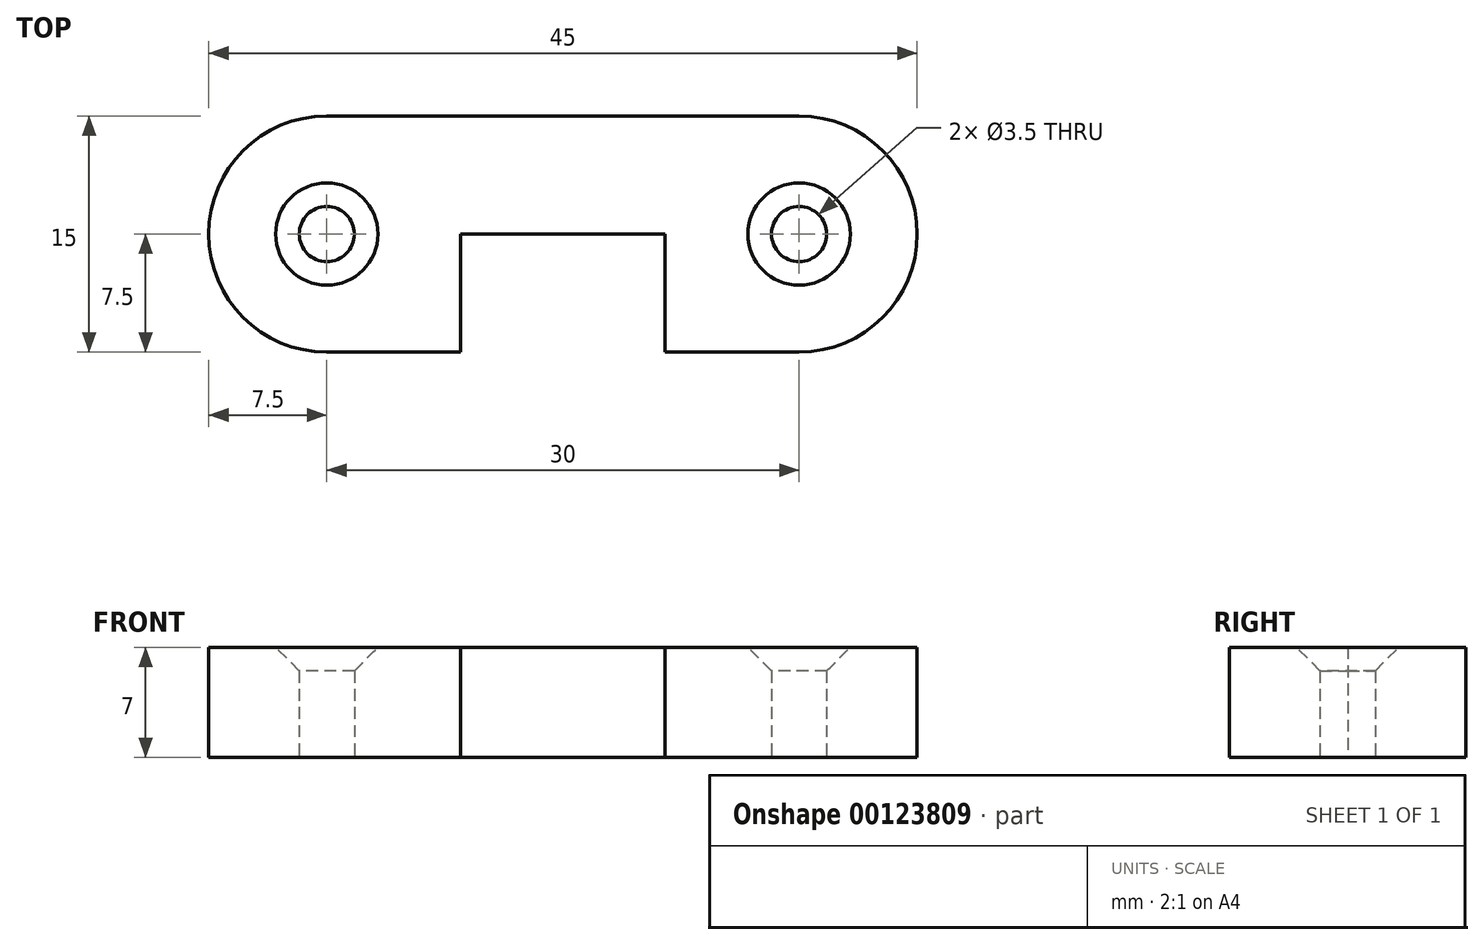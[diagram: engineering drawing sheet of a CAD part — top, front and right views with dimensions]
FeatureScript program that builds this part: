
annotation { "Feature Type Name" : "Feature", "Feature Type Description" : "" }
export const myFeature = defineFeature(function(context is Context, id is Id, definition is map)
    precondition{}
    {
        {
            var Q0;
            Q0=qCreatedBy(makeId("Top.planeOp"),FACE);
            var sketch = newSketch(context, id + "F0", { "sketchPlane" : qUnion([Q0])});
            skLineSegment(sketch, "E0.bottom", {"start": v(7.5, 7.5) * mm, "end": v(-7.5, 7.5) * mm});
            skLineSegment(sketch, "E0.top", {"start": v(7.5, -7.5) * mm, "end": v(-7.5, -7.5) * mm});
            skLineSegment(sketch, "E0.left", {"start": v(7.5, 7.5) * mm, "end": v(7.5, -7.5) * mm});
            skLineSegment(sketch, "E0.right", {"start": v(-7.5, 7.5) * mm, "end": v(-7.5, -7.5) * mm});
            skPoint(sketch, "E0.middle", {"position": v(0, 0) * mm});
            skLineSegment(sketch, "E1", {"start": v(-7.5, 7.5) * mm, "end": v(-15, 7.5) * mm});
            skLineSegment(sketch, "E2", {"start": v(-7.5, -7.5) * mm, "end": v(-15, -7.5) * mm});
            skLineSegment(sketch, "E3", {"start": v(7.5, -7.5) * mm, "end": v(15, -7.5) * mm});
            skLineSegment(sketch, "E4", {"start": v(7.5, 7.5) * mm, "end": v(15, 7.5) * mm});
            skArc(sketch, "E5", {"start": v(-15, 7.5) * mm, "mid": v(-22.5, 0) * mm, "end": v(-15, -7.5) * mm});
            skPoint(sketch, "E5.first.point", {"position": v(-7.5, 0) * mm});
            skPoint(sketch, "E5.second.point", {"position": v(-15, 7.5) * mm});
            skPoint(sketch, "E5.third.point", {"position": v(-15, -7.5) * mm});
            skArc(sketch, "E6", {"start": v(15, -7.5) * mm, "mid": v(22.5, 0) * mm, "end": v(15, 7.5) * mm});
            skPoint(sketch, "E6.first.point", {"position": v(7.5, 0) * mm});
            skPoint(sketch, "E6.second.point", {"position": v(15, 7.5) * mm});
            skPoint(sketch, "E6.third.point", {"position": v(15, -7.5) * mm});
            skCircle(sketch, "E7", {"center": v(-15, 0) * mm, "radius": 1.75 * mm});
            skCircle(sketch, "E8", {"center": v(15, 0) * mm, "radius": 1.75 * mm});
            skLineSegment(sketch, "E9.bottom", {"start": v(6.5, 0) * mm, "end": v(-6.5, 0) * mm});
            skLineSegment(sketch, "E9.top", {"start": v(6.5, -15) * mm, "end": v(-6.5, -15) * mm});
            skLineSegment(sketch, "E9.left", {"start": v(6.5, 0) * mm, "end": v(6.5, -15) * mm});
            skLineSegment(sketch, "E9.right", {"start": v(-6.5, 0) * mm, "end": v(-6.5, -15) * mm});
            skPoint(sketch, "E9.middle", {"position": v(0, -7.5) * mm});
            skSolve(sketch);
        }
        {
            var Q0;
            Q0=makeQuery(id+"F0.imprint","IMPRINT",FACE,{"disambiguationData":[TD([[makeQuery(id+"F0.imprint","IMPRINT",EDGE,{"derivedFrom":sQuery(id+"F0.wireOp",EDGE,"E0.right")}),-1.0]])]});
            var Q1;
            Q1=makeQuery(id+"F0.imprint","IMPRINT",FACE,{"disambiguationData":[TD([[makeQuery(id+"F0.imprint","IMPRINT",EDGE,{"derivedFrom":sQuery(id+"F0.wireOp",EDGE,"E0.bottom")}),1.0]])]});
            var Q2;
            Q2=makeQuery(id+"F0.imprint","IMPRINT",FACE,{"disambiguationData":[TD([[makeQuery(id+"F0.imprint","IMPRINT",EDGE,{"derivedFrom":sQuery(id+"F0.wireOp",EDGE,"E0.left")}),1.0]])]});
            extrude(context, id + "F1", {"entities" : qUnion([Q0, Q1, Q2]), "depth" : 7 * mm});
        }
        {
            var Q0;
            Q0=makeQuery(id+"F1.opExtrude","CAP_EDGE",EDGE,{"disambiguationData":[OSD([sQuery(id+"F0.wireOp",EDGE,"E7")])],"isStart":false});
            var Q1;
            Q1=makeQuery(id+"F1.opExtrude","CAP_EDGE",EDGE,{"disambiguationData":[OSD([sQuery(id+"F0.wireOp",EDGE,"E8")])],"isStart":false});
            chamfer(context, id + "F2", {"entities" : qUnion([Q0, Q1]), "width" : 1.5 * mm, "tangentPropagation" : true});
        }
    });
